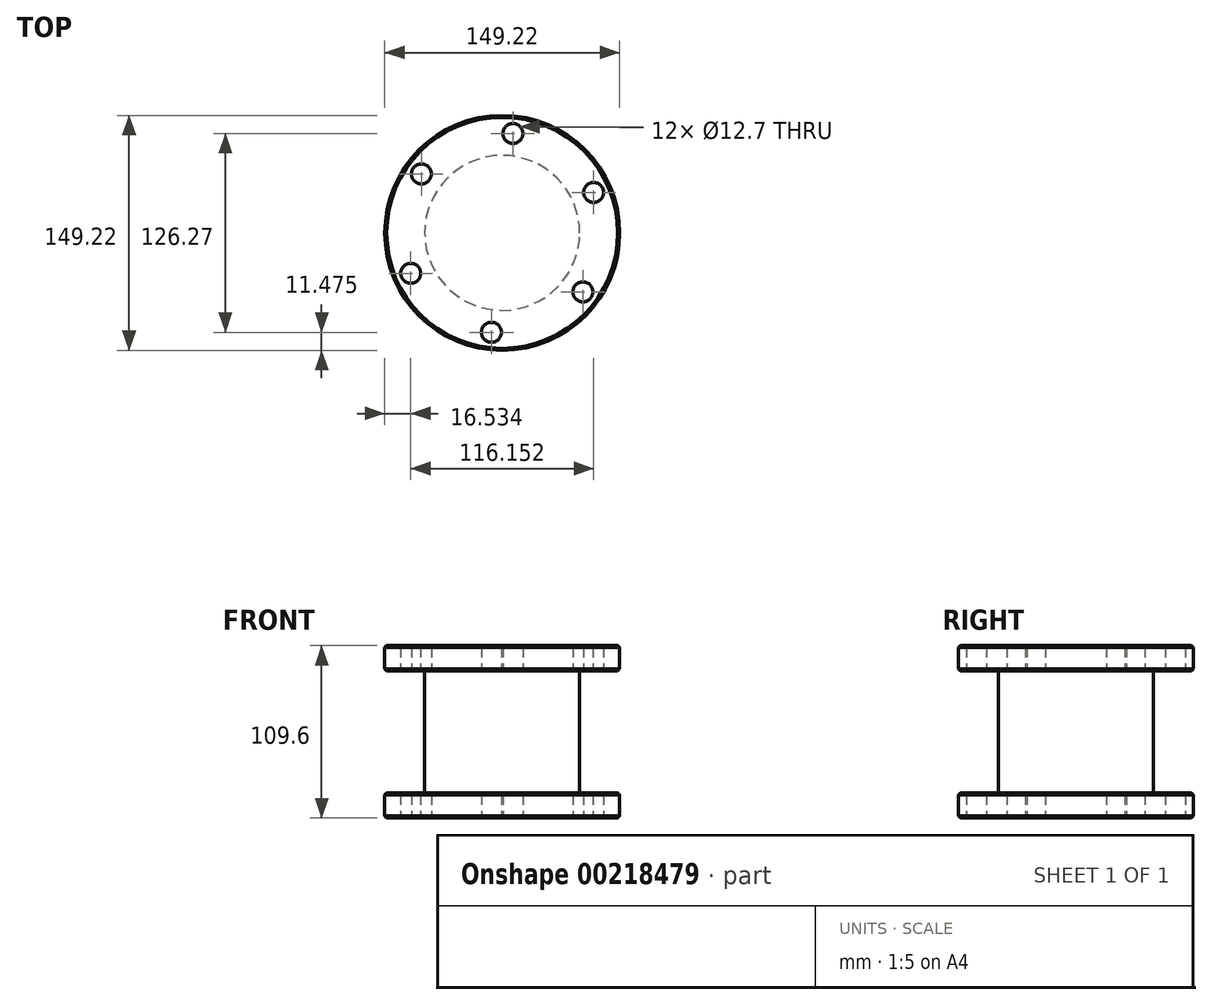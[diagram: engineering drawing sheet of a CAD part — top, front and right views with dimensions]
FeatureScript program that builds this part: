
annotation { "Feature Type Name" : "Feature", "Feature Type Description" : "" }
export const myFeature = defineFeature(function(context is Context, id is Id, definition is map)
    precondition{}
    {
        {
            var Q0;
            Q0=qCreatedBy(makeId("Top.planeOp"),FACE);
            var sketch = newSketch(context, id + "F0", { "sketchPlane" : qUnion([Q0])});
            skCircle(sketch, "E0", {"center": v(0, 0) * mm, "radius": 74.61 * mm});
            skSolve(sketch);
        }
        {
            var Q0;
            Q0 = qSketchRegion(id + "F0", true);
            extrude(context, id + "F1", {"entities" : qUnion([Q0]), "depth" : 16 * mm});
        }
        {
            var Q0;
            Q0=makeQuery(id+"F1.opExtrude","CAP_FACE",FACE,{"disambiguationData":[OSD([sQuery(id+"F0.wireOp",EDGE,"E0")])],"isStart":false});
            var sketch = newSketch(context, id + "F2", { "sketchPlane" : qUnion([Q0])});
            skCircle(sketch, "E1", {"center": v(0, 0) * mm, "radius": 49.21 * mm});
            skSolve(sketch);
        }
        {
            var Q0;
            Q0 = qSketchRegion(id + "F2", true);
            extrude(context, id + "F3", {"entities" : qUnion([Q0]), "operationType" : NewBodyOperationType.ADD, "depth" : 77.6 * mm});
        }
        {
            var Q0;
            Q0=makeQuery(id+"F3.opExtrude","CAP_FACE",FACE,{"disambiguationData":[OSD([sQuery(id+"F2.wireOp",EDGE,"E1")])],"isStart":false});
            var sketch = newSketch(context, id + "F4", { "sketchPlane" : qUnion([Q0])});
            skCircle(sketch, "E2", {"center": v(0, 0) * mm, "radius": 74.61 * mm});
            skSolve(sketch);
        }
        {
            var Q0;
            Q0 = qSketchRegion(id + "F4", true);
            extrude(context, id + "F5", {"entities" : qUnion([Q0]), "operationType" : NewBodyOperationType.ADD, "depth" : 16 * mm});
        }
        {
            var Q0;
            Q0=makeQuery(id+"F5.opExtrude","CAP_EDGE",EDGE,{"disambiguationData":[OSD([sQuery(id+"F4.wireOp",EDGE,"E2")])],"isStart":true});
            var Q1;
            Q1=makeQuery(id+"F5.opExtrude","CAP_EDGE",EDGE,{"disambiguationData":[OSD([sQuery(id+"F4.wireOp",EDGE,"E2")])],"isStart":false});
            var Q2;
            Q2=makeQuery(id+"F1.opExtrude","CAP_EDGE",EDGE,{"disambiguationData":[OSD([sQuery(id+"F0.wireOp",EDGE,"E0")])],"isStart":false});
            var Q3;
            Q3=makeQuery(id+"F1.opExtrude","CAP_EDGE",EDGE,{"disambiguationData":[OSD([sQuery(id+"F0.wireOp",EDGE,"E0")])],"isStart":true});
            chamfer(context, id + "F6", {"entities" : qUnion([Q0, Q1, Q2, Q3]), "width" : 1.27 * mm, "tangentPropagation" : true});
        }
        {
            var Q0;
            Q0=makeQuery(id+"F1.opExtrude","CAP_FACE",FACE,{"disambiguationData":[OSD([sQuery(id+"F0.wireOp",EDGE,"E0")])],"isStart":true});
            var sketch = newSketch(context, id + "F7", { "sketchPlane" : qUnion([Q0])});
            skPoint(sketch, "E3", {"position": v(-58.08, 25.68) * mm});
            skPoint(sketch, "E4.1.0", {"position": v(-51.28, -37.46) * mm});
            skPoint(sketch, "E4.2.0", {"position": v(6.8, -63.13) * mm});
            skPoint(sketch, "E4.3.0", {"position": v(58.08, -25.68) * mm});
            skPoint(sketch, "E4.4.0", {"position": v(51.28, 37.46) * mm});
            skPoint(sketch, "E4.5.0", {"position": v(-6.8, 63.13) * mm});
            skPoint(sketch, "E4.center", {"position": v(0, 0) * mm});
            skSolve(sketch);
        }
        {
            var Q0;
            Q0=sQuery(id+"F7.wireOp",VERTEX,"E4.1.0");
            var Q1;
            Q1=sQuery(id+"F7.wireOp",VERTEX,"E3");
            var Q2;
            Q2=sQuery(id+"F7.wireOp",VERTEX,"E4.5.0");
            var Q3;
            Q3=sQuery(id+"F7.wireOp",VERTEX,"E4.4.0");
            var Q4;
            Q4=sQuery(id+"F7.wireOp",VERTEX,"E4.3.0");
            var Q5;
            Q5=sQuery(id+"F7.wireOp",VERTEX,"E4.2.0");
            var Q6;
            Q6=makeQuery(id+"F1.opExtrude","SWEPT_BODY",BODY,{"disambiguationData":[OSD([sQuery(id+"F0.wireOp",EDGE,"E0")])]});
            hole(context, id + "F8", {"style" : HoleStyle.SIMPLE, "endStyle" : HoleEndStyle.BLIND, "holeDiameter" : 12.7 * mm, "holeDepth" : 127 * mm, "startFromSketch" : true, "locations" : qUnion([Q0, Q1, Q2, Q3, Q4, Q5]), "scope" : qUnion([Q6])});
        }
    });
